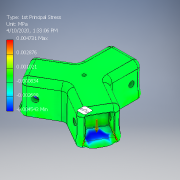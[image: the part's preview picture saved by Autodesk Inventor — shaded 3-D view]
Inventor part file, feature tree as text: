
AUTODESK INVENTOR PART (.ipt)
format: ipt  version: 2019.4 (Build 234330000, 330)  size: 274,944 bytes
history: native  units: mm
features: extrude x4, sketch x4, pattern_circular x3, fillet x3
ambient origin geometry x8: Origin, YZ Plane, XZ Plane, XY Plane, X Axis, Y Axis, Z Axis, Center Point
bodies: Solid1 (feature_tree)
feature tree (14):
  extrude  "Extrusion1"  Depth=40.0mm
  extrude  "Extrusion6"  Depth=30.0mm
  pattern_circular  "Circular Pattern4"  Count=3  [1 undecoded]
  extrude  "Extrusion7"  Depth=21.0mm
  pattern_circular  "Circular Pattern5"  [2 undecoded]
  extrude  "Extrusion8"  Depth=30.0mm TaperAngle=360.0deg
  pattern_circular  "Circular Pattern6"  [2 undecoded]
  fillet  "Fillet5"  Radius=5.5mm
  fillet  "Fillet6"  Radius=30.0mm
  fillet  "Fillet7"  Radius=30.0mm
  sketch  "Sketch1"  dims[d0=30.0mm d1=40.0mm]
  sketch  "Sketch6"  dims[d2=30.0mm d3=0.0mm d32=3.0mm d33=30.0mm d34=0.0mm]
  sketch  "Sketch7"  dims[d35=30.0mm d36=360.0deg d38=21.0mm]
  sketch  "Sketch8"  dims[d39=21.0mm d40=15.0mm d41=0.0mm d42=30.0mm d43=360.0deg d45=10.0mm d46=5.5mm d47=30.0mm d48=0.0mm d49=30.0mm d50=360.0deg d52=5.0mm d53=5.0mm d54=4.0mm]
note: 5 required parameter values undecoded (feature->parameter linkage not recoverable at this tier; creation-order binding heuristic only, values carry confidence <= 0.55)
